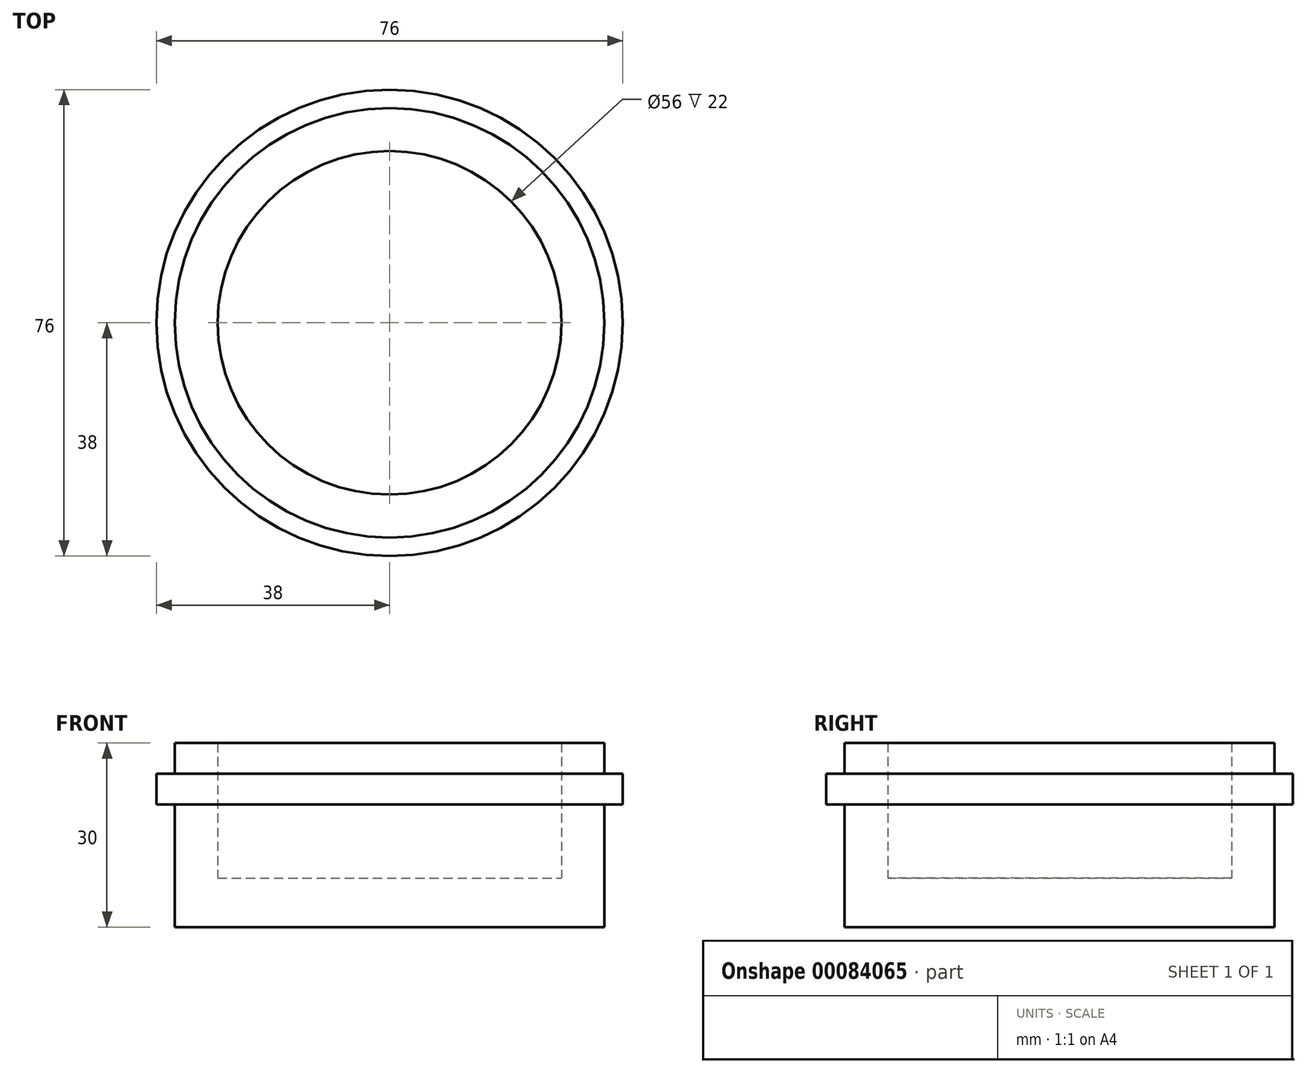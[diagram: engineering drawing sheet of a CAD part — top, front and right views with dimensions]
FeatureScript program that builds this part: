
annotation { "Feature Type Name" : "Feature", "Feature Type Description" : "" }
export const myFeature = defineFeature(function(context is Context, id is Id, definition is map)
    precondition{}
    {
        {
            var Q0;
            Q0=qCreatedBy(makeId("Front.planeOp"),FACE);
            var sketch = newSketch(context, id + "F0", { "sketchPlane" : qUnion([Q0])});
            skLineSegment(sketch, "E0", {"start": v(38, 17) * mm, "end": v(38, 12) * mm});
            skLineSegment(sketch, "E1", {"start": v(38, 12) * mm, "end": v(35, 12) * mm});
            skLineSegment(sketch, "E2", {"start": v(35, 12) * mm, "end": v(35, -8) * mm});
            skLineSegment(sketch, "E3", {"start": v(35, -8) * mm, "end": v(28, -8) * mm});
            skLineSegment(sketch, "E4", {"start": v(28, -8) * mm, "end": v(0, -8) * mm});
            skLineSegment(sketch, "E5", {"start": v(0, -8) * mm, "end": v(0, 0) * mm});
            skLineSegment(sketch, "E6", {"start": v(0, 0) * mm, "end": v(28, 0) * mm});
            skLineSegment(sketch, "E7", {"start": v(28, 0) * mm, "end": v(28, 17) * mm});
            skLineSegment(sketch, "E8", {"start": v(38, 17) * mm, "end": v(35, 17) * mm});
            skLineSegment(sketch, "E9", {"start": v(35, 17) * mm, "end": v(35, 22) * mm});
            skLineSegment(sketch, "E10", {"start": v(35, 22) * mm, "end": v(28, 22) * mm});
            skLineSegment(sketch, "E11", {"start": v(28, 22) * mm, "end": v(28, 17) * mm});
            skSolve(sketch);
        }
        {
            var Q0;
            Q0=makeQuery(id+"F0.imprint","IMPRINT",FACE,{"disambiguationData":[TD([[makeQuery(id+"F0.imprint","IMPRINT",EDGE,{"derivedFrom":sQuery(id+"F0.wireOp",EDGE,"E0")}),-1.0]])]});
            var Q1;
            Q1=sQuery(id+"F0.wireOp",EDGE,"E5");
            revolve(context, id + "F1", {"entities" : qUnion([Q0]), "axis" : qUnion([Q1]), "revolveType" : RevolveType.FULL});
        }
    });
